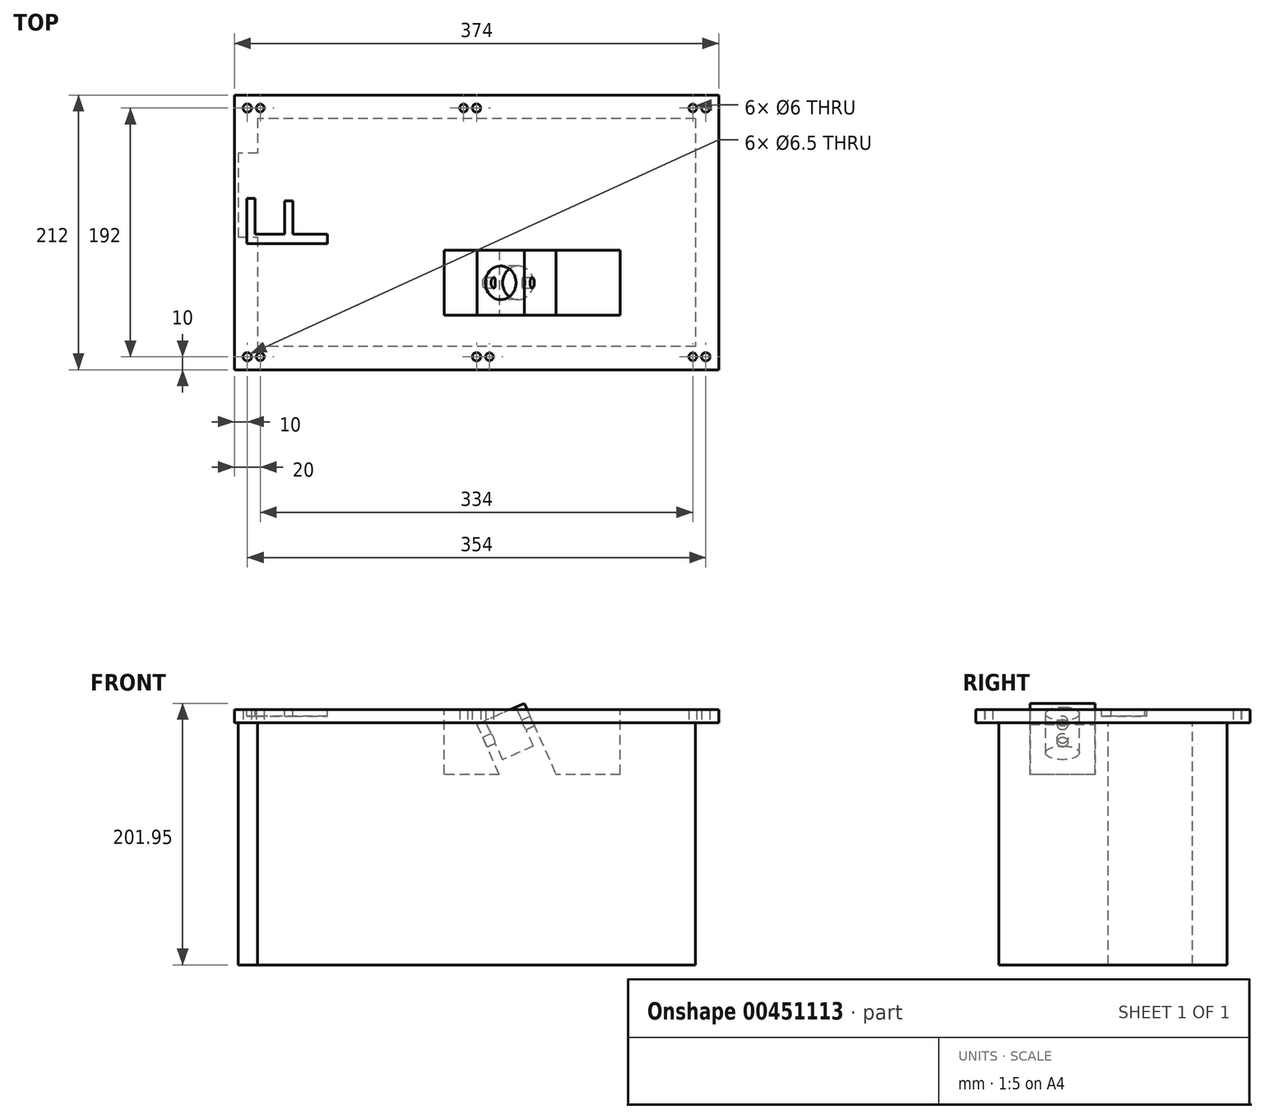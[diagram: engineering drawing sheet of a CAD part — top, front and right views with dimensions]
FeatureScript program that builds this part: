
annotation { "Feature Type Name" : "Feature", "Feature Type Description" : "" }
export const myFeature = defineFeature(function(context is Context, id is Id, definition is map)
    precondition{}
    {
        {
            var Q0;
            Q0=qCreatedBy(makeId("Top.planeOp"),FACE);
            var sketch = newSketch(context, id + "F0", { "sketchPlane" : qUnion([Q0])});
            skLineSegment(sketch, "E0.bottom", {"start": v(187, -106) * mm, "end": v(-187, -106) * mm});
            skLineSegment(sketch, "E0.top", {"start": v(187, 106) * mm, "end": v(-187, 106) * mm});
            skLineSegment(sketch, "E0.left", {"start": v(187, -106) * mm, "end": v(187, 106) * mm});
            skLineSegment(sketch, "E0.right", {"start": v(-187, -106) * mm, "end": v(-187, 106) * mm});
            skPoint(sketch, "E0.middle", {"position": v(0, 0) * mm});
            skSolve(sketch);
        }
        {
            var Q0;
            Q0=qSketchRegion(id+"F0",true);
            extrude(context, id + "F1", {"entities" : qUnion([Q0]), "depth" : 10 * mm});
        }
        {
            var Q0;
            Q0=makeQuery(id+"F1.opExtrude","CAP_FACE",FACE,{"disambiguationData":[OSD([sQuery(id+"F0.wireOp",EDGE,"E0.bottom"),sQuery(id+"F0.wireOp",EDGE,"E0.top"),sQuery(id+"F0.wireOp",EDGE,"E0.left"),sQuery(id+"F0.wireOp",EDGE,"E0.right")])],"isStart":true});
            var sketch = newSketch(context, id + "F2", { "sketchPlane" : qUnion([Q0])});
            skLineSegment(sketch, "E1.bottom", {"start": v(169, -88) * mm, "end": v(-169, -88) * mm});
            skLineSegment(sketch, "E1.top", {"start": v(169, 88) * mm, "end": v(-169, 88) * mm});
            skLineSegment(sketch, "E1.left", {"start": v(169, -88) * mm, "end": v(169, 88) * mm});
            skLineSegment(sketch, "E1.right", {"start": v(-169, -88) * mm, "end": v(-169, 88) * mm});
            skPoint(sketch, "E1.middle", {"position": v(0, 0) * mm});
            skLineSegment(sketch, "E2", {"start": v(-169, -61.3) * mm, "end": v(-184, -61.3) * mm});
            skLineSegment(sketch, "E3", {"start": v(-184, -61.3) * mm, "end": v(-184, 3.7) * mm});
            skLineSegment(sketch, "E4", {"start": v(-184, 3.7) * mm, "end": v(-169, 3.7) * mm});
            skSolve(sketch);
        }
        {
            var Q0;
            Q0=qSketchRegion(id+"F2",true);
            extrude(context, id + "F3", {"entities" : qUnion([Q0]), "operationType" : NewBodyOperationType.ADD, "depth" : 187 * mm});
        }
        {
            var Q0;
            Q0=makeQuery(id+"F1.opExtrude","CAP_FACE",FACE,{"disambiguationData":[OSD([sQuery(id+"F0.wireOp",EDGE,"E0.bottom"),sQuery(id+"F0.wireOp",EDGE,"E0.top"),sQuery(id+"F0.wireOp",EDGE,"E0.left"),sQuery(id+"F0.wireOp",EDGE,"E0.right")])],"isStart":false});
            var sketch = newSketch(context, id + "F4", { "sketchPlane" : qUnion([Q0])});
            skLineSegment(sketch, "E5.bottom", {"start": v(110.87, -63.9) * mm, "end": v(-24.87, -63.9) * mm});
            skLineSegment(sketch, "E5.top", {"start": v(110.87, -13.9) * mm, "end": v(-24.87, -13.9) * mm});
            skLineSegment(sketch, "E5.left", {"start": v(110.87, -63.9) * mm, "end": v(110.87, -13.9) * mm});
            skLineSegment(sketch, "E5.right", {"start": v(-24.87, -63.9) * mm, "end": v(-24.87, -13.9) * mm});
            skPoint(sketch, "E5.middle", {"position": v(43, -38.9) * mm});
            skSolve(sketch);
        }
        {
            var Q0;
            Q0=qSketchRegion(id+"F4",true);
            extrude(context, id + "F5", {"entities" : qUnion([Q0]), "operationType" : NewBodyOperationType.REMOVE, "oppositeDirection" : true, "depth" : 50 * mm});
        }
        {
            var Q0;
            {var subQ0=sQuery(id+"F0.wireOp",EDGE,"E0.left");var subQ1=sQuery(id+"F0.wireOp",EDGE,"E0.top");var subQ2=sQuery(id+"F0.wireOp",EDGE,"E0.right");var subQ3=sQuery(id+"F0.wireOp",EDGE,"E0.bottom");Q0=makeQuery(id+"F5.boolean.opBoolean","SPLIT",FACE,{"disambiguationData":[TD([makeQuery(id+"F1.opExtrude","SWEPT_FACE",FACE,{"disambiguationData":[OSD([subQ3])]})])],"derivedFrom":makeQuery(id+"F1.opExtrude","CAP_FACE",FACE,{"disambiguationData":[OSD([subQ3,subQ1,subQ0,subQ2])],"isStart":false})});}
            var sketch = newSketch(context, id + "F6", { "sketchPlane" : qUnion([Q0])});
            skPoint(sketch, "E6", {"position": v(-177, 96) * mm});
            skPoint(sketch, "E7", {"position": v(-167, 96) * mm});
            skPoint(sketch, "E8", {"position": v(-10, 96) * mm});
            skPoint(sketch, "E9", {"position": v(0, 96) * mm});
            skPoint(sketch, "E10", {"position": v(167, 96) * mm});
            skPoint(sketch, "E11", {"position": v(177, 96) * mm});
            skPoint(sketch, "E12.MirrorP", {"position": v(177, -96) * mm});
            skPoint(sketch, "E13.MirrorP", {"position": v(167, -96) * mm});
            skPoint(sketch, "E14.MirrorP", {"position": v(-167, -96) * mm});
            skPoint(sketch, "E15.MirrorP", {"position": v(-177, -96) * mm});
            skPoint(sketch, "E16", {"position": v(0, -96) * mm});
            skPoint(sketch, "E17", {"position": v(10, -96) * mm});
            skSolve(sketch);
        }
        {
            var Q0;
            Q0=sQuery(id+"F6.wireOp",VERTEX,"E7");
            var Q1;
            Q1=sQuery(id+"F6.wireOp",VERTEX,"E14.MirrorP");
            var Q2;
            Q2=sQuery(id+"F6.wireOp",VERTEX,"E13.MirrorP");
            var Q3;
            Q3=sQuery(id+"F6.wireOp",VERTEX,"E10");
            var Q4;
            Q4=sQuery(id+"F6.wireOp",VERTEX,"E8");
            var Q5;
            Q5=sQuery(id+"F6.wireOp",VERTEX,"E17");
            var Q6;
            Q6=makeQuery(id+"F1.opExtrude","SWEPT_BODY",BODY,{"disambiguationData":[OSD([sQuery(id+"F0.wireOp",EDGE,"E0.bottom"),sQuery(id+"F0.wireOp",EDGE,"E0.top"),sQuery(id+"F0.wireOp",EDGE,"E0.left"),sQuery(id+"F0.wireOp",EDGE,"E0.right")])]});
            hole(context, id + "F7", {"style" : HoleStyle.SIMPLE, "endStyle" : HoleEndStyle.BLIND, "holeDiameter" : 6 * mm, "holeDepth" : 10 * mm, "tappedDepth" : 12 * mm, "tapClearance" : 3, "locations" : qUnion([Q0, Q1, Q2, Q3, Q4, Q5]), "scope" : qUnion([Q6])});
        }
        {
            var Q0;
            Q0=sQuery(id+"F6.wireOp",VERTEX,"E6");
            var Q1;
            Q1=sQuery(id+"F6.wireOp",VERTEX,"E15.MirrorP");
            var Q2;
            Q2=sQuery(id+"F6.wireOp",VERTEX,"E16");
            var Q3;
            Q3=sQuery(id+"F6.wireOp",VERTEX,"E9");
            var Q4;
            Q4=sQuery(id+"F6.wireOp",VERTEX,"E11");
            var Q5;
            Q5=sQuery(id+"F6.wireOp",VERTEX,"E12.MirrorP");
            var Q6;
            Q6=makeQuery(id+"F1.opExtrude","SWEPT_BODY",BODY,{"disambiguationData":[OSD([sQuery(id+"F0.wireOp",EDGE,"E0.bottom"),sQuery(id+"F0.wireOp",EDGE,"E0.top"),sQuery(id+"F0.wireOp",EDGE,"E0.left"),sQuery(id+"F0.wireOp",EDGE,"E0.right")])]});
            hole(context, id + "F8", {"style" : HoleStyle.SIMPLE, "endStyle" : HoleEndStyle.BLIND, "holeDiameter" : 6.5 * mm, "holeDepth" : 10 * mm, "tappedDepth" : 12 * mm, "tapClearance" : 3, "locations" : qUnion([Q0, Q1, Q2, Q3, Q4, Q5]), "scope" : qUnion([Q6])});
        }
        {
            var Q0;
            Q0=makeQuery(id+"F6.imprint","IMPRINT",FACE,{"disambiguationData":[TD([[makeQuery(id+"F6.imprint","IMPRINT",EDGE,{"derivedFrom":makeQuery(id+"F1.opExtrude","CAP_EDGE",EDGE,{"disambiguationData":[OSD([sQuery(id+"F0.wireOp",EDGE,"E0.bottom")])],"isStart":false})}),-1.0]])]});
            var sketch = newSketch(context, id + "F9", { "sketchPlane" : qUnion([Q0])});
            skText(sketch, "E18", { "text": "F", "fontName": "OpenSans-Regular.ttf"});
            const initialGuessF9  = {"E18": [-0.11521, -0.01712, 0, 1, 0.06278]};
            skSetInitialGuess(sketch, initialGuessF9);
            skSolve(sketch);
        }
        {
            var Q0;
            Q0 = qSketchRegion(id + "F9", true);
            extrude(context, id + "F10", {"entities" : qUnion([Q0]), "operationType" : NewBodyOperationType.REMOVE, "oppositeDirection" : true, "depth" : 5 * mm, "offsetDistance" : 25 * mm});
        }
        {
            var Q0;
            Q0=makeQuery(id+"F5.boolean.opBoolean","COPY",FACE,{"derivedFrom":makeQuery(id+"F5.opExtrude","SWEPT_FACE",FACE,{"disambiguationData":[OSD([sQuery(id+"F4.wireOp",EDGE,"E5.top")])]})});
            cPlane(context, id + "F11", {"entities" : qUnion([Q0]), "cplaneType" : CPlaneType.OFFSET, "offset" : 25 * mm, "width" : 150 * mm, "height" : 150 * mm});
        }
        {
            var Q0;
            Q0=qCreatedBy(id+"F11.planeOp",FACE);
            var sketch = newSketch(context, id + "F12", { "sketchPlane" : qUnion([Q0])});
            skLineSegment(sketch, "E19", {"start": v(36.87, 14.95) * mm, "end": v(61.27, -39.87) * mm});
            skLineSegment(sketch, "E20", {"start": v(61.27, -39.87) * mm, "end": v(24.73, -56.13) * mm});
            skLineSegment(sketch, "E21", {"start": v(24.73, -56.13) * mm, "end": v(0.32, -1.32) * mm});
            skLineSegment(sketch, "E22", {"start": v(0.32, -1.32) * mm, "end": v(36.87, 14.95) * mm});
            skPoint(sketch, "E23", {"position": v(43, -48) * mm});
            skLineSegment(sketch, "E24", {"start": v(43, -48) * mm, "end": v(43, 95.44) * mm, "construction": true});
            skSolve(sketch);
        }
        {
            var Q0;
            Q0 = qSketchRegion(id + "F12", true);
            extrude(context, id + "F13", {"entities" : qUnion([Q0]), "operationType" : NewBodyOperationType.ADD, "depth" : 50 * mm, "offsetDistance" : 25 * mm, "symmetric" : true});
        }
        {
            var Q0;
            Q0=makeQuery(id+"F13.opExtrude","SWEPT_FACE",FACE,{"disambiguationData":[OSD([sQuery(id+"F12.wireOp",EDGE,"E22")])]});
            var sketch = newSketch(context, id + "F14", { "sketchPlane" : qUnion([Q0])});
            skCircle(sketch, "E25", {"center": v(19.76, -38.9) * mm, "radius": 13 * mm});
            skSolve(sketch);
        }
        {
            var Q0;
            Q0 = qSketchRegion(id + "F14", true);
            extrude(context, id + "F15", {"entities" : qUnion([Q0]), "operationType" : NewBodyOperationType.REMOVE, "oppositeDirection" : true, "depth" : 33 * mm, "offsetDistance" : 25 * mm});
        }
        {
            var Q0;
            Q0=makeQuery(id+"F13.opExtrude","SWEPT_FACE",FACE,{"disambiguationData":[OSD([sQuery(id+"F12.wireOp",EDGE,"E19")])]});
            var sketch = newSketch(context, id + "F16", { "sketchPlane" : qUnion([Q0])});
            skCircle(sketch, "E26", {"center": v(-38.9, -16.34) * mm, "radius": 4.1 * mm});
            skSolve(sketch);
        }
        {
            var Q0;
            Q0 = qSketchRegion(id + "F16", true);
            extrude(context, id + "F17", {"entities" : qUnion([Q0]), "operationType" : NewBodyOperationType.REMOVE, "oppositeDirection" : true, "depth" : 47 * mm, "offsetDistance" : 25 * mm});
        }
    });
